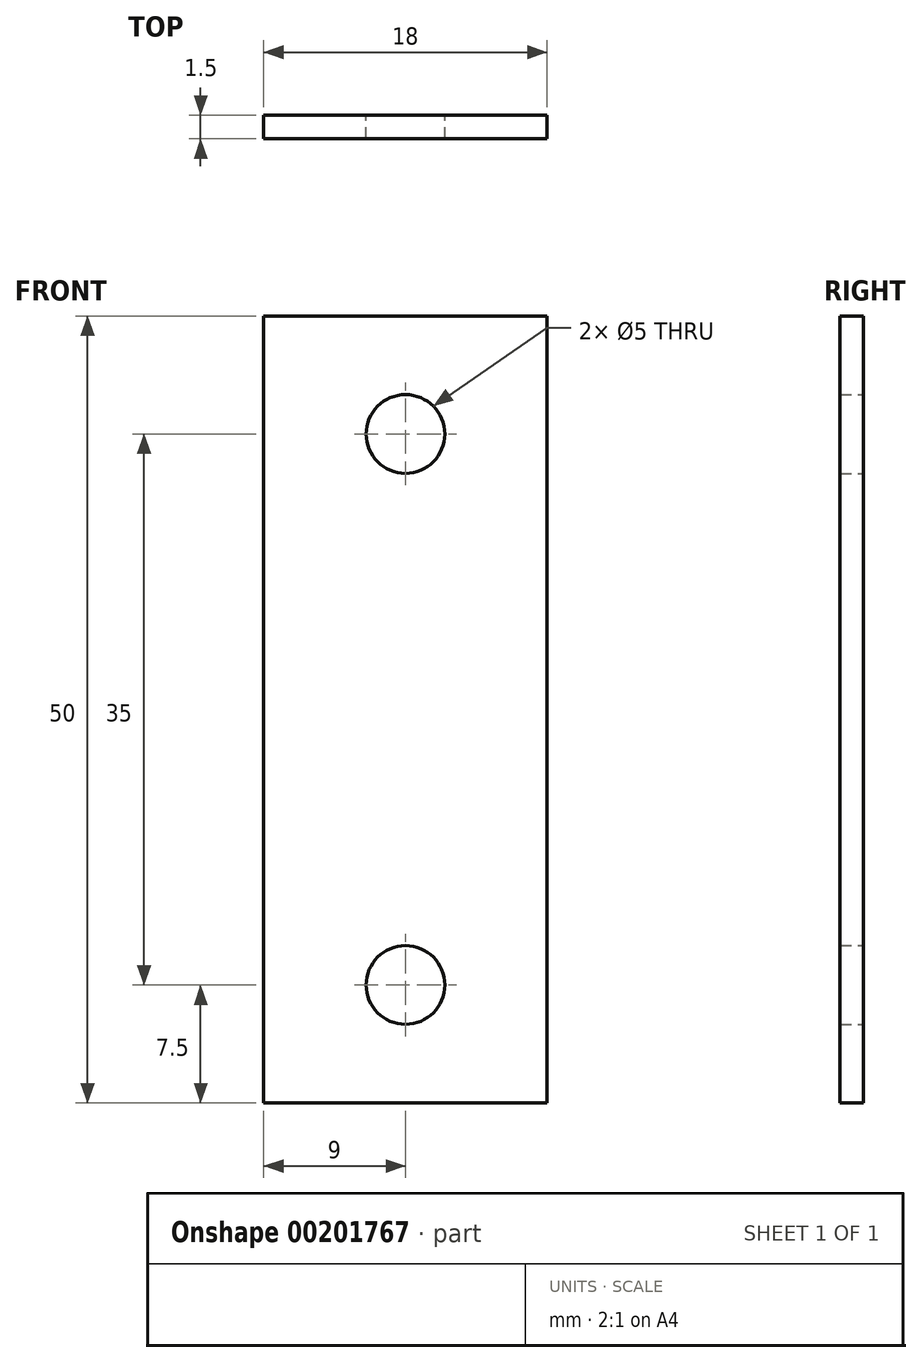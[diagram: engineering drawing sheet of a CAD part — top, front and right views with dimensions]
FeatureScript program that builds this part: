
annotation { "Feature Type Name" : "Feature", "Feature Type Description" : "" }
export const myFeature = defineFeature(function(context is Context, id is Id, definition is map)
    precondition{}
    {
        {
            var Q0;
            Q0=qCreatedBy(makeId("Front.planeOp"),FACE);
            var sketch = newSketch(context, id + "F0", { "sketchPlane" : qUnion([Q0])});
            skLineSegment(sketch, "E0", {"start": v(-18, 0) * mm, "end": v(-18, 50) * mm});
            skLineSegment(sketch, "E1", {"start": v(-18, 50) * mm, "end": v(0, 50) * mm});
            skCircle(sketch, "E2", {"center": v(-9, 42.5) * mm, "radius": 2.5 * mm});
            skCircle(sketch, "E3", {"center": v(-9, 7.5) * mm, "radius": 2.5 * mm});
            skLineSegment(sketch, "E4", {"start": v(0, 50) * mm, "end": v(0, 0) * mm});
            skLineSegment(sketch, "E5", {"start": v(0, 0) * mm, "end": v(-18, 0) * mm});
            skSolve(sketch);
        }
        {
            var Q0;
            Q0=makeQuery(id+"F0.imprint","IMPRINT",FACE,{"disambiguationData":[TD([[makeQuery(id+"F0.imprint","IMPRINT",EDGE,{"derivedFrom":sQuery(id+"F0.wireOp",EDGE,"ZEJhduRj-ZByP-Te0h-TF62-EHsjinoBiS8H")}),-1.0]])]});
            var Q1;
            Q1=makeQuery(id+"F0.imprint","IMPRINT",FACE,{"disambiguationData":[TD([[makeQuery(id+"F0.imprint","IMPRINT",EDGE,{"derivedFrom":sQuery(id+"F0.wireOp",EDGE,"E0")}),-1.0]])]});
            extrude(context, id + "F1", {"entities" : qUnion([Q0, Q1]), "depth" : 1.5 * mm, "offsetDistance" : 25 * mm});
        }
    });
